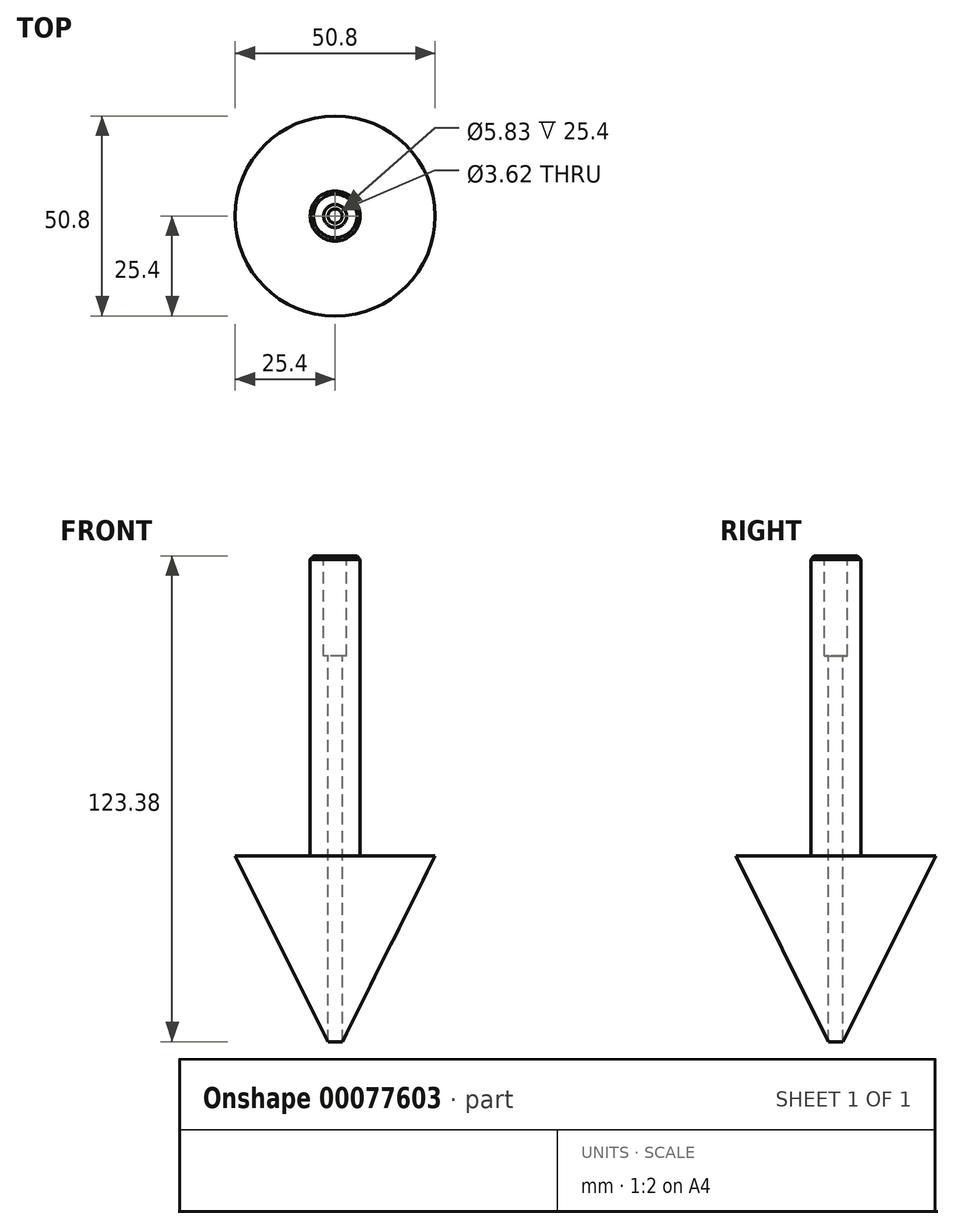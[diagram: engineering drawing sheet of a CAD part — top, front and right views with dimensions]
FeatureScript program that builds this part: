
annotation { "Feature Type Name" : "Feature", "Feature Type Description" : "" }
export const myFeature = defineFeature(function(context is Context, id is Id, definition is map)
    precondition{}
    {
        {
            var Q0;
            Q0=qCreatedBy(makeId("Front.planeOp"),FACE);
            var sketch = newSketch(context, id + "F0", { "sketchPlane" : qUnion([Q0])});
            skLineSegment(sketch, "E0", {"start": v(0, 0) * mm, "end": v(0, -50.8) * mm});
            skLineSegment(sketch, "E1", {"start": v(0, -50.8) * mm, "end": v(-25.4, 0) * mm});
            skLineSegment(sketch, "E2", {"start": v(-25.4, 0) * mm, "end": v(-6.35, 0) * mm});
            skLineSegment(sketch, "E3", {"start": v(-6.35, 0) * mm, "end": v(-6.35, 76.2) * mm});
            skLineSegment(sketch, "E4", {"start": v(-6.35, 76.2) * mm, "end": v(0, 76.2) * mm});
            skLineSegment(sketch, "E5", {"start": v(0, 76.2) * mm, "end": v(0, 0) * mm});
            skSolve(sketch);
        }
        {
            var Q0;
            Q0 = qSketchRegion(id + "F0", true);
            var Q1;
            Q1=sQuery(id+"F0.wireOp",EDGE,"E5");
            revolve(context, id + "F1", {"entities" : qUnion([Q0]), "axis" : qUnion([Q1]), "revolveType" : RevolveType.FULL});
        }
        {
            var Q0;
            Q0=makeQuery(id+"F1.opRevolve","SWEPT_FACE",FACE,{"disambiguationData":[OSD([sQuery(id+"F0.wireOp",EDGE,"E4")])]});
            var sketch = newSketch(context, id + "F2", { "sketchPlane" : qUnion([Q0])});
            skCircle(sketch, "E6", {"center": v(0, 0) * mm, "radius": 2.92 * mm});
            skSolve(sketch);
        }
        {
            var Q0;
            Q0 = qSketchRegion(id + "F2", true);
            extrude(context, id + "F3", {"entities" : qUnion([Q0]), "operationType" : NewBodyOperationType.REMOVE, "oppositeDirection" : true, "depth" : 25.4 * mm});
        }
        {
            var Q0;
            Q0=makeQuery(id+"F1.opRevolve","SWEPT_EDGE",EDGE,{"disambiguationData":[OSD([sQuery(id+"F0.wireOp",EDGE,"E3"),sQuery(id+"F0.wireOp",EDGE,"E4")])]});
            chamfer(context, id + "F4", {"entities" : qUnion([Q0]), "width" : 0.81 * mm, "tangentPropagation" : true});
        }
        {
            var Q0;
            Q0=makeQuery(id+"F1.opRevolve","SWEPT_FACE",FACE,{"disambiguationData":[OSD([sQuery(id+"F0.wireOp",EDGE,"E4")])]});
            var sketch = newSketch(context, id + "F5", { "sketchPlane" : qUnion([Q0])});
            skCircle(sketch, "E7", {"center": v(0, 0) * mm, "radius": 1.8 * mm});
            skSolve(sketch);
        }
        {
            var Q0;
            Q0 = qSketchRegion(id + "F5", true);
            extrude(context, id + "F6", {"entities" : qUnion([Q0]), "operationType" : NewBodyOperationType.REMOVE, "endBound" : BoundingType.THROUGH_ALL, "oppositeDirection" : true, "depth" : 25.4 * mm});
        }
    });
